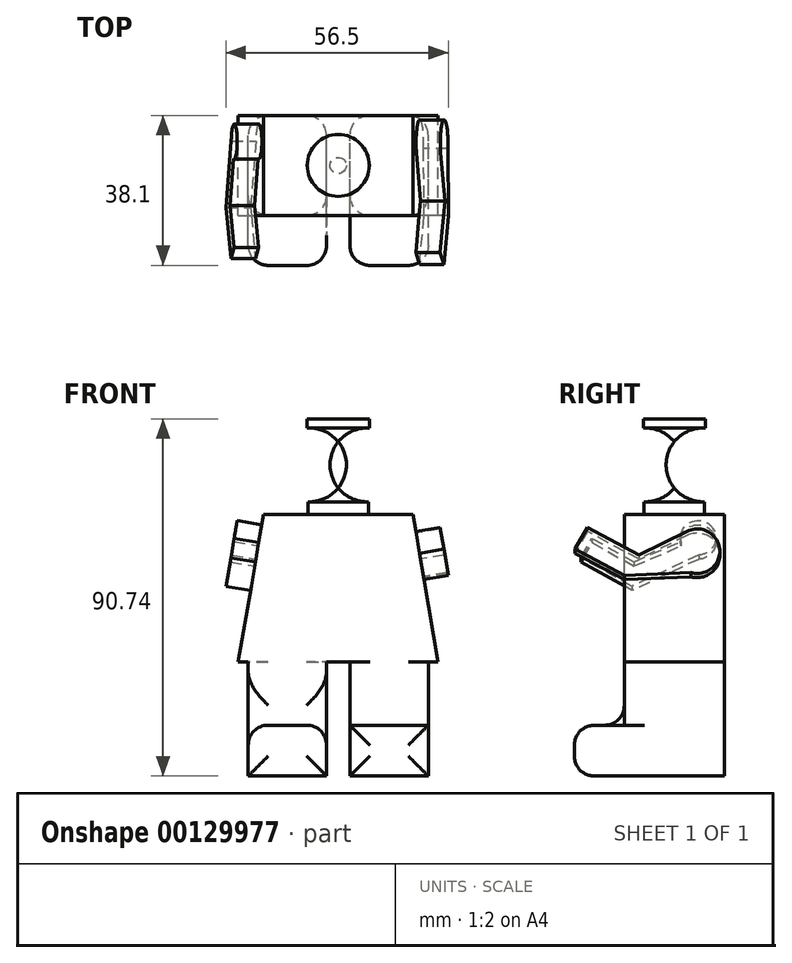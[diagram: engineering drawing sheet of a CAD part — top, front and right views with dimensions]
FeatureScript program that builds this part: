
annotation { "Feature Type Name" : "Feature", "Feature Type Description" : "" }
export const myFeature = defineFeature(function(context is Context, id is Id, definition is map)
    precondition{}
    {
        {
            var Q0;
            Q0=qCreatedBy(makeId("Front.planeOp"),FACE);
            var sketch = newSketch(context, id + "F0", { "sketchPlane" : qUnion([Q0])});
            skLineSegment(sketch, "E0", {"start": v(25.4, 0) * mm, "end": v(18.95, 37.55) * mm});
            skLineSegment(sketch, "E1", {"start": v(18.95, 37.55) * mm, "end": v(0, 37.55) * mm});
            skLineSegment(sketch, "E2", {"start": v(0, 37.55) * mm, "end": v(0, 0) * mm});
            skLineSegment(sketch, "E3", {"start": v(25.4, 0) * mm, "end": v(0, 0) * mm});
            skLineSegment(sketch, "E4", {"start": v(22.87, 0) * mm, "end": v(22.87, -28.95) * mm});
            skLineSegment(sketch, "E5", {"start": v(22.87, -28.95) * mm, "end": v(2.94, -28.95) * mm});
            skLineSegment(sketch, "E6", {"start": v(2.94, -28.95) * mm, "end": v(2.94, 0) * mm});
            skLineSegment(sketch, "E7.MirrorCS", {"start": v(-25.4, 0) * mm, "end": v(0, 0) * mm});
            skLineSegment(sketch, "E8.MirrorCS", {"start": v(-18.95, 37.55) * mm, "end": v(0, 37.55) * mm});
            skLineSegment(sketch, "E9.MirrorCS", {"start": v(-25.4, 0) * mm, "end": v(-18.95, 37.55) * mm});
            skLineSegment(sketch, "E10.MirrorCS", {"start": v(-22.87, 0) * mm, "end": v(-22.87, -28.95) * mm});
            skLineSegment(sketch, "E11.MirrorCS", {"start": v(-22.87, -28.95) * mm, "end": v(-2.94, -28.95) * mm});
            skLineSegment(sketch, "E12.MirrorCS", {"start": v(-2.94, -28.95) * mm, "end": v(-2.94, 0) * mm});
            skSolve(sketch);
        }
        {
            var Q0;
            Q0 = qSketchRegion(id + "F0", true);
            extrude(context, id + "F1", {"entities" : qUnion([Q0]), "endBound" : BoundingType.SYMMETRIC, "depth" : 25.4 * mm});
        }
        {
            var Q0;
            Q0=makeQuery(id+"F1.opExtrude","CAP_FACE",FACE,{"disambiguationData":[OSD([sQuery(id+"F0.wireOp",EDGE,"E0"),sQuery(id+"F0.wireOp",EDGE,"E1"),sQuery(id+"F0.wireOp",EDGE,"E3"),sQuery(id+"F0.wireOp",EDGE,"E4"),sQuery(id+"F0.wireOp",EDGE,"E5"),sQuery(id+"F0.wireOp",EDGE,"E6"),sQuery(id+"F0.wireOp",EDGE,"E7.MirrorCS"),sQuery(id+"F0.wireOp",EDGE,"E8.MirrorCS"),sQuery(id+"F0.wireOp",EDGE,"E9.MirrorCS"),sQuery(id+"F0.wireOp",EDGE,"E10.MirrorCS"),sQuery(id+"F0.wireOp",EDGE,"E11.MirrorCS"),sQuery(id+"F0.wireOp",EDGE,"E12.MirrorCS")])],"isStart":false});
            var sketch = newSketch(context, id + "F2", { "sketchPlane" : qUnion([Q0])});
            skLineSegment(sketch, "E13", {"start": v(2.94, -16.04) * mm, "end": v(22.87, -16.04) * mm});
            skLineSegment(sketch, "E14", {"start": v(-2.94, -16.04) * mm, "end": v(-22.87, -16.04) * mm});
            skLineSegment(sketch, "E15", {"start": v(22.87, -16.04) * mm, "end": v(22.87, -28.95) * mm});
            skLineSegment(sketch, "E16", {"start": v(22.87, -28.95) * mm, "end": v(2.94, -28.95) * mm});
            skLineSegment(sketch, "E17", {"start": v(2.94, -28.95) * mm, "end": v(2.94, -16.04) * mm});
            skLineSegment(sketch, "E18", {"start": v(-2.94, -16.04) * mm, "end": v(-2.94, -28.95) * mm});
            skLineSegment(sketch, "E19", {"start": v(-2.94, -28.95) * mm, "end": v(-22.87, -28.95) * mm});
            skLineSegment(sketch, "E20", {"start": v(-22.87, -28.95) * mm, "end": v(-22.87, -16.04) * mm});
            skSolve(sketch);
        }
        {
            var Q0;
            Q0 = qSketchRegion(id + "F2", true);
            extrude(context, id + "F3", {"entities" : qUnion([Q0]), "operationType" : NewBodyOperationType.ADD, "depth" : 12.7 * mm});
        }
        {
            var Q0;
            Q0=makeQuery(id+"F3.opExtrude","CAP_FACE",FACE,{"disambiguationData":[OSD([sQuery(id+"F2.wireOp",EDGE,"E14"),sQuery(id+"F2.wireOp",EDGE,"E18"),sQuery(id+"F2.wireOp",EDGE,"E19"),sQuery(id+"F2.wireOp",EDGE,"E20")])],"isStart":false});
            var Q1;
            Q1=makeQuery(id+"F3.opExtrude","CAP_FACE",FACE,{"disambiguationData":[OSD([sQuery(id+"F2.wireOp",EDGE,"E13"),sQuery(id+"F2.wireOp",EDGE,"E15"),sQuery(id+"F2.wireOp",EDGE,"E16"),sQuery(id+"F2.wireOp",EDGE,"E17")])],"isStart":false});
            var Q2;
            Q2=makeQuery(id+"F3.opExtrude","CAP_EDGE",EDGE,{"disambiguationData":[OSD([sQuery(id+"F2.wireOp",EDGE,"E13")])],"isStart":true});
            var Q3;
            Q3=makeQuery(id+"F3.opExtrude","SWEPT_FACE",FACE,{"disambiguationData":[OSD([sQuery(id+"F2.wireOp",EDGE,"E14")])]});
            var Q4;
            Q4=makeQuery(id+"F1.opExtrude","CAP_EDGE",EDGE,{"disambiguationData":[OSD([sQuery(id+"F0.wireOp",EDGE,"E4")])],"isStart":true});
            var Q5;
            Q5=makeQuery(id+"F1.opExtrude","CAP_EDGE",EDGE,{"disambiguationData":[OSD([sQuery(id+"F0.wireOp",EDGE,"E6")])],"isStart":true});
            var Q6;
            Q6=makeQuery(id+"F1.opExtrude","CAP_EDGE",EDGE,{"disambiguationData":[OSD([sQuery(id+"F0.wireOp",EDGE,"E10.MirrorCS")])],"isStart":true});
            var Q7;
            Q7=makeQuery(id+"F1.opExtrude","CAP_EDGE",EDGE,{"disambiguationData":[OSD([sQuery(id+"F0.wireOp",EDGE,"E12.MirrorCS")])],"isStart":true});
            var Q8;
            Q8=makeQuery(id+"F1.opExtrude","CAP_EDGE",EDGE,{"disambiguationData":[OSD([sQuery(id+"F0.wireOp",EDGE,"E4")])],"isStart":false});
            var Q9;
            Q9=makeQuery(id+"F1.opExtrude","CAP_EDGE",EDGE,{"disambiguationData":[OSD([sQuery(id+"F0.wireOp",EDGE,"E6")])],"isStart":false});
            fillet(context, id + "F4", {"entities" : qUnion([Q0, Q1, Q2, Q3, Q4, Q5, Q6, Q7, Q8, Q9]), "radius" : 5.08 * mm, "tangentPropagation" : true, "allowEdgeOverflow" : false});
        }
        {
            var Q0;
            Q0=qCreatedBy(makeId("Front.planeOp"),FACE);
            var sketch = newSketch(context, id + "F5", { "sketchPlane" : qUnion([Q0])});
            skArc(sketch, "E21", {"start": v(7.69, 40.74) * mm, "mid": v(16.69, 50.02) * mm, "end": v(7.88, 59.47) * mm});
            skLineSegment(sketch, "E22", {"start": v(7.69, 40.74) * mm, "end": v(7.69, 33.12) * mm});
            skLineSegment(sketch, "E23", {"start": v(7.69, 33.12) * mm, "end": v(0, 33.12) * mm});
            skLineSegment(sketch, "E24", {"start": v(0, 33.12) * mm, "end": v(0, 61.79) * mm});
            skLineSegment(sketch, "E25", {"start": v(0, 61.79) * mm, "end": v(7.88, 61.79) * mm});
            skLineSegment(sketch, "E26", {"start": v(7.88, 61.79) * mm, "end": v(7.88, 59.47) * mm});
            skLineSegment(sketch, "E27.MirrorCS", {"start": v(0, 61.79) * mm, "end": v(-7.88, 61.79) * mm});
            skLineSegment(sketch, "E28.MirrorCS", {"start": v(-7.88, 61.79) * mm, "end": v(-7.88, 59.47) * mm});
            skArc(sketch, "E29.MirrorCS", {"start": v(-7.69, 40.74) * mm, "mid": v(-16.69, 50.02) * mm, "end": v(-7.88, 59.47) * mm});
            skLineSegment(sketch, "E30.MirrorCS", {"start": v(-7.69, 40.74) * mm, "end": v(-7.69, 33.12) * mm});
            skLineSegment(sketch, "E31.MirrorCS", {"start": v(-7.69, 33.12) * mm, "end": v(0, 33.12) * mm});
            skSolve(sketch);
        }
        {
            var Q0;
            Q0=makeQuery(id+"F5.imprint","IMPRINT",FACE,{"disambiguationData":[TD([[makeQuery(id+"F5.imprint","IMPRINT",EDGE,{"derivedFrom":sQuery(id+"F5.wireOp",EDGE,"E21")}),1.0]])]});
            var Q1;
            Q1=sQuery(id+"F5.wireOp",EDGE,"E24");
            revolve(context, id + "F6", {"operationType" : NewBodyOperationType.ADD, "entities" : qUnion([Q0]), "axis" : qUnion([Q1]), "revolveType" : RevolveType.FULL});
        }
        {
            var Q0;
            Q0=makeQuery(id+"F1.opExtrude","SWEPT_FACE",FACE,{"disambiguationData":[OSD([sQuery(id+"F0.wireOp",EDGE,"E0")])]});
            var sketch = newSketch(context, id + "F7", { "sketchPlane" : qUnion([Q0])});
            skArc(sketch, "E32", {"start": v(4.27, 17.7) * mm, "mid": v(11.54, 23.76) * mm, "end": v(3.27, 28.36) * mm});
            skLineSegment(sketch, "E33", {"start": v(3.27, 28.36) * mm, "end": v(-9.02, 22.25) * mm});
            skLineSegment(sketch, "E34", {"start": v(-9.02, 22.25) * mm, "end": v(-22.1, 29.4) * mm});
            skLineSegment(sketch, "E35", {"start": v(-22.1, 29.4) * mm, "end": v(-25.17, 23.76) * mm});
            skLineSegment(sketch, "E36", {"start": v(-25.17, 23.76) * mm, "end": v(-12.7, 16.96) * mm});
            skPoint(sketch, "E36.endSnap0", {"position": v(-12.7, 14.75) * mm});
            skLineSegment(sketch, "E37", {"start": v(-12.7, 16.96) * mm, "end": v(4.27, 17.7) * mm});
            skSolve(sketch);
        }
        {
            var Q0;
            Q0 = qSketchRegion(id + "F7", true);
            extrude(context, id + "F8", {"entities" : qUnion([Q0]), "operationType" : NewBodyOperationType.ADD, "depth" : 6.25 * mm});
        }
        {
            var Q0;
            Q0=makeQuery(id+"F1.opExtrude","SWEPT_FACE",FACE,{"disambiguationData":[OSD([sQuery(id+"F0.wireOp",EDGE,"E9.MirrorCS")])]});
            var sketch = newSketch(context, id + "F9", { "sketchPlane" : qUnion([Q0])});
            skArc(sketch, "E38", {"start": v(-1.73, 25.7) * mm, "mid": v(-8.77, 30.2) * mm, "end": v(-6.25, 22.23) * mm});
            skLineSegment(sketch, "E39", {"start": v(-6.25, 22.23) * mm, "end": v(10.74, 14.17) * mm});
            skLineSegment(sketch, "E40", {"start": v(10.74, 14.17) * mm, "end": v(23.71, 21.51) * mm});
            skLineSegment(sketch, "E41", {"start": v(23.71, 21.51) * mm, "end": v(20.9, 26.5) * mm});
            skLineSegment(sketch, "E42", {"start": v(20.9, 26.5) * mm, "end": v(10.21, 20.44) * mm});
            skLineSegment(sketch, "E43", {"start": v(10.21, 20.44) * mm, "end": v(-1.73, 25.7) * mm});
            skSolve(sketch);
        }
        {
            var Q0;
            Q0=makeQuery(id+"F9.imprint","IMPRINT",FACE,{"disambiguationData":[TD([[makeQuery(id+"F9.imprint","IMPRINT",EDGE,{"derivedFrom":sQuery(id+"F9.wireOp",EDGE,"E38")}),1.0]])]});
            var Q1;
            {var subQ0=sQuery(id+"F9.wireOp",EDGE,"E41");Q1=makeQuery(id+"F9.imprint","IMPRINT",FACE,{"disambiguationData":[TD([[makeQuery(id+"F9.imprint","IMPRINT",EDGE,{"derivedFrom":subQ0}),1.0]])]});}
            extrude(context, id + "F10", {"entities" : qUnion([Q0, Q1]), "operationType" : NewBodyOperationType.ADD, "depth" : 6.35 * mm});
        }
    });
